# Revit family: Indoor_Wall Lamp_Santa&Cole_Wally Cesta
name_source: partatom
category: Luminarias
revit_build: Autodesk Revit 2018 (Build: 20170223_1515(x64)
units: mm (PartAtom-declared; Revit-internal decimal feet)

## family parameters
Compartido = No
Corte con vacíos al cargar = No
Cota de conector redondo = Diámetro de uso
Número OmniClass = 23.80.70.00
Origen de luz = Sí
Punto de cálculo de habitación = No
Se basa en plano de trabajo = Sí
Siempre vertical = Sí
Tipo de pieza = Normal
Título OmniClass = Lighting

## types (4) — shared parameters
Archivo de red fotométrica = Wally Cesta WALWB01 (CL004A22F002G).IES
Assembly instructions - CE = https://www.santacole.com
Assembly instructions - UL = https://www.santacole.com
Cambio de temperatura de color de luz atenuada = <Ninguno>
Carga aparente = 6 VA
Elevación por defecto = 1219 mm
Fabricante = Santa & Cole
Filtro de color = 16777215
Manufacturer website = https://www.santacole.com
Modelo = Wally Cesta
Technical Information = https://www.santacole.com
URL = https://www.santacole.com
Voltaje (90-305 V) = 220 V
Ángulo de inclinación = -90.00°

## per-type parameters (varying)
| type | Code | Material | UL |
| Wally Cesta UL - Blanco | WALWB02 | Santa&Cole - White Matte Finish | Sí |
| Wally Cesta UL - Negro | WALWB01 | Santa&Cole - Black Matte Finish | Sí |
| Wally Cesta CE - Negro | WALWB01 | Santa&Cole - Black Matte Finish | No |
| Wally Cesta CE - Blanco | WALWB02 | Santa&Cole - White Matte Finish | No |
